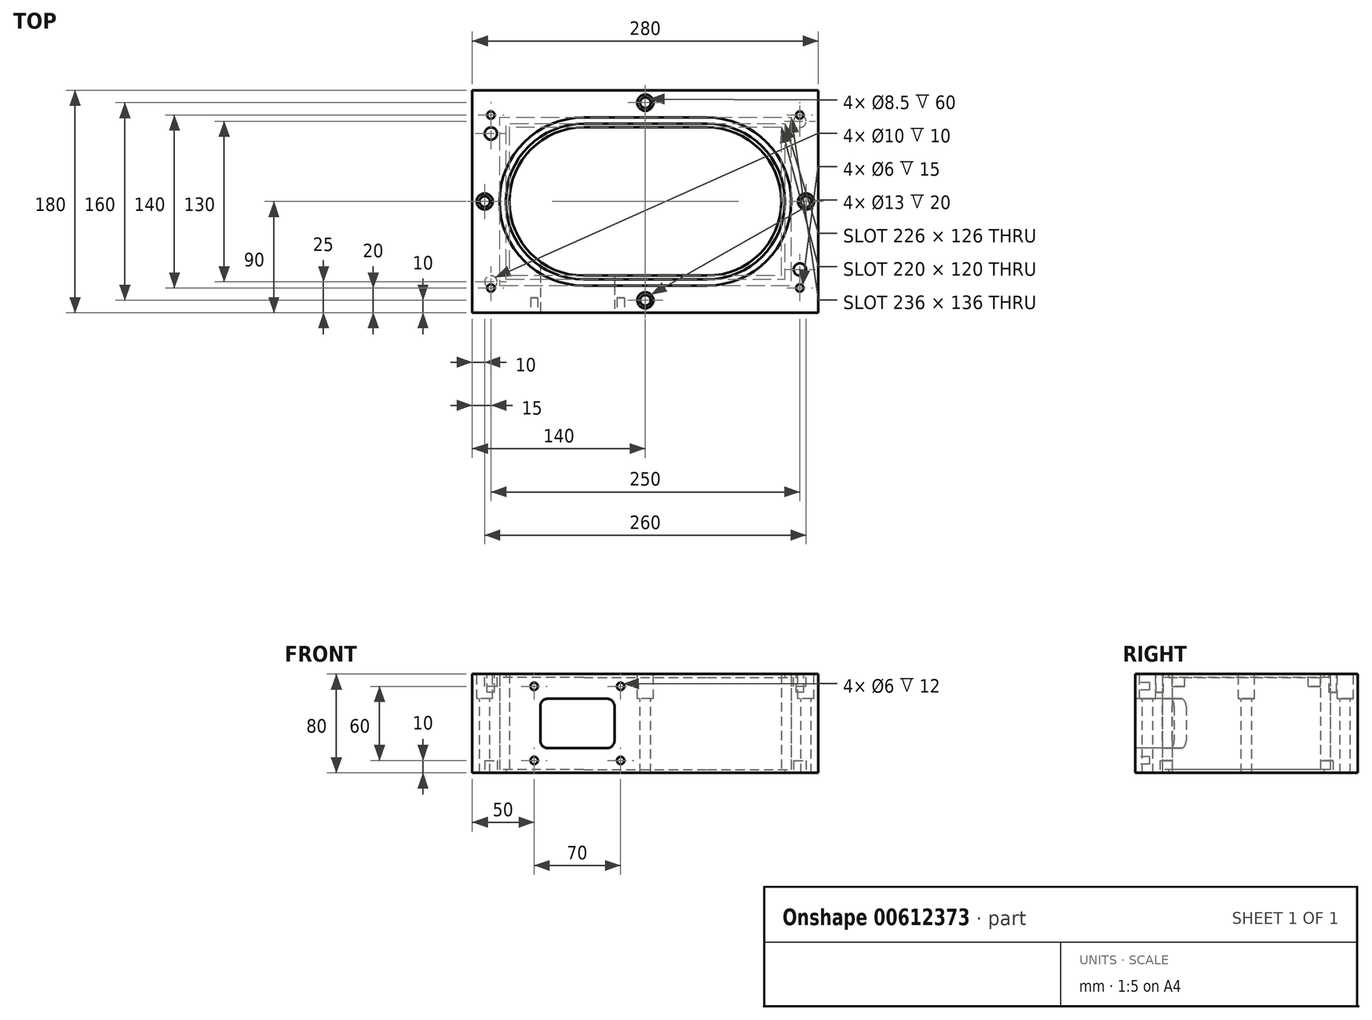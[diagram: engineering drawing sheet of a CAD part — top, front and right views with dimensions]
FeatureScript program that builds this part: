
annotation { "Feature Type Name" : "Feature", "Feature Type Description" : "" }
export const myFeature = defineFeature(function(context is Context, id is Id, definition is map)
    precondition{}
    {
        {
            var Q0;
            Q0=qCreatedBy(makeId("Top.planeOp"),FACE);
            var sketch = newSketch(context, id + "F0", { "sketchPlane" : qUnion([Q0])});
            skLineSegment(sketch, "E0.bottom", {"start": v(-140, 90) * mm, "end": v(140, 90) * mm});
            skLineSegment(sketch, "E0.top", {"start": v(-140, -90) * mm, "end": v(140, -90) * mm});
            skLineSegment(sketch, "E0.left", {"start": v(-140, 90) * mm, "end": v(-140, -90) * mm});
            skLineSegment(sketch, "E0.right", {"start": v(140, 90) * mm, "end": v(140, -90) * mm});
            skArc(sketch, "E1", {"start": v(-50, 60) * mm, "mid": v(-110, 0) * mm, "end": v(-50, -60) * mm});
            skArc(sketch, "E2", {"start": v(50, -60) * mm, "mid": v(110, 0) * mm, "end": v(50, 60) * mm});
            skArc(sketch, "E3", {"start": v(-50, 63) * mm, "mid": v(-113, 0) * mm, "end": v(-50, -63) * mm});
            skArc(sketch, "E4", {"start": v(50, -63) * mm, "mid": v(113, 0) * mm, "end": v(50, 63) * mm});
            skLineSegment(sketch, "E5", {"start": v(-50, 68) * mm, "end": v(50, 68) * mm});
            skLineSegment(sketch, "E6", {"start": v(50, 63) * mm, "end": v(-50, 63) * mm});
            skLineSegment(sketch, "E7", {"start": v(-50, 60) * mm, "end": v(50, 60) * mm});
            skLineSegment(sketch, "E8", {"start": v(-50, -60) * mm, "end": v(50, -60) * mm});
            skLineSegment(sketch, "E9", {"start": v(50, -63) * mm, "end": v(-50, -63) * mm});
            skLineSegment(sketch, "E10", {"start": v(-50, -68) * mm, "end": v(50, -68) * mm});
            skArc(sketch, "E11.trimOffspring", {"start": v(-50, 68) * mm, "mid": v(-118, 0) * mm, "end": v(-50, -68) * mm});
            skArc(sketch, "E12.trimOffspring", {"start": v(50, -68) * mm, "mid": v(118, 0) * mm, "end": v(50, 68) * mm});
            skSolve(sketch);
        }
        {
            var Q0;
            Q0=makeQuery(id+"F0.imprint","IMPRINT",FACE,{"disambiguationData":[TD([[makeQuery(id+"F0.imprint","IMPRINT",EDGE,{"derivedFrom":sQuery(id+"F0.wireOp",EDGE,"E0.bottom")}),-1.0]])]});
            extrude(context, id + "F1", {"entities" : qUnion([Q0]), "depth" : 40 * mm, "offsetDistance" : 25 * mm, "hasSecondDirection" : true, "secondDirectionOppositeDirection" : true, "secondDirectionDepth" : 40 * mm});
        }
        {
            var Q0;
            Q0=makeQuery(id+"F0.imprint","IMPRINT",FACE,{"disambiguationData":[TD([[makeQuery(id+"F0.imprint","IMPRINT",EDGE,{"derivedFrom":sQuery(id+"F0.wireOp",EDGE,"E3")}),-1.0]])]});
            extrude(context, id + "F2", {"entities" : qUnion([Q0]), "depth" : 37.3 * mm, "offsetDistance" : 25 * mm, "hasSecondDirection" : true, "secondDirectionOppositeDirection" : true, "secondDirectionDepth" : 37.3 * mm});
        }
        {
            var Q0;
            Q0=makeQuery(id+"F0.imprint","IMPRINT",FACE,{"disambiguationData":[TD([[makeQuery(id+"F0.imprint","IMPRINT",EDGE,{"derivedFrom":sQuery(id+"F0.wireOp",EDGE,"E1")}),-1.0]])]});
            extrude(context, id + "F3", {"entities" : qUnion([Q0]), "operationType" : NewBodyOperationType.ADD, "depth" : 40 * mm, "offsetDistance" : 25 * mm, "hasSecondDirection" : true, "secondDirectionOppositeDirection" : true, "secondDirectionDepth" : 40 * mm});
        }
        {
            var Q0;
            Q0=makeQuery(id+"F1.opExtrude","CAP_FACE",FACE,{"disambiguationData":[OSD([sQuery(id+"F0.wireOp",EDGE,"E0.bottom"),sQuery(id+"F0.wireOp",EDGE,"E0.top"),sQuery(id+"F0.wireOp",EDGE,"E0.left"),sQuery(id+"F0.wireOp",EDGE,"E0.right"),sQuery(id+"F0.wireOp",EDGE,"E5"),sQuery(id+"F0.wireOp",EDGE,"E10"),sQuery(id+"F0.wireOp",EDGE,"E11.trimOffspring"),sQuery(id+"F0.wireOp",EDGE,"E12.trimOffspring")])],"isStart":false});
            var sketch = newSketch(context, id + "F4", { "sketchPlane" : qUnion([Q0])});
            skCircle(sketch, "E13", {"center": v(-130, 0) * mm, "radius": 6.5 * mm});
            skCircle(sketch, "E14", {"center": v(130, 0) * mm, "radius": 6.5 * mm});
            skCircle(sketch, "E15", {"center": v(0, -80) * mm, "radius": 6.5 * mm});
            skPoint(sketch, "E15.centerSnap0", {"position": v(0, -68) * mm});
            skCircle(sketch, "E16", {"center": v(0, 80) * mm, "radius": 6.5 * mm});
            skCircle(sketch, "E17", {"center": v(-130, 0) * mm, "radius": 4.25 * mm});
            skCircle(sketch, "E18", {"center": v(0, -80) * mm, "radius": 4.25 * mm});
            skCircle(sketch, "E19", {"center": v(130, 0) * mm, "radius": 4.25 * mm});
            skCircle(sketch, "E20", {"center": v(0, 80) * mm, "radius": 4.25 * mm});
            skCircle(sketch, "E21", {"center": v(-125, -70) * mm, "radius": 3 * mm});
            skCircle(sketch, "E22", {"center": v(125, -70) * mm, "radius": 3 * mm});
            skCircle(sketch, "E23", {"center": v(125, 70) * mm, "radius": 3 * mm});
            skCircle(sketch, "E24", {"center": v(-125, 70) * mm, "radius": 3 * mm});
            skCircle(sketch, "E25", {"center": v(-125, 55) * mm, "radius": 5 * mm});
            skCircle(sketch, "E26", {"center": v(125, -55) * mm, "radius": 5 * mm});
            skSolve(sketch);
        }
        {
            var Q0;
            Q0=makeQuery(id+"F4.imprint","IMPRINT",FACE,{"disambiguationData":[TD([[makeQuery(id+"F4.imprint","IMPRINT",EDGE,{"derivedFrom":sQuery(id+"F4.wireOp",EDGE,"E25")}),1.0]])]});
            var Q1;
            Q1=makeQuery(id+"F4.imprint","IMPRINT",FACE,{"disambiguationData":[TD([[makeQuery(id+"F4.imprint","IMPRINT",EDGE,{"derivedFrom":sQuery(id+"F4.wireOp",EDGE,"E26")}),1.0]])]});
            extrude(context, id + "F5", {"entities" : qUnion([Q0, Q1]), "operationType" : NewBodyOperationType.REMOVE, "oppositeDirection" : true, "depth" : 10 * mm, "offsetDistance" : 25 * mm});
        }
        {
            var Q0;
            Q0=makeQuery(id+"F4.imprint","IMPRINT",FACE,{"disambiguationData":[TD([[makeQuery(id+"F4.imprint","IMPRINT",EDGE,{"derivedFrom":sQuery(id+"F4.wireOp",EDGE,"E20")}),1.0]])]});
            var Q1;
            Q1=makeQuery(id+"F4.imprint","IMPRINT",FACE,{"disambiguationData":[TD([[makeQuery(id+"F4.imprint","IMPRINT",EDGE,{"derivedFrom":sQuery(id+"F4.wireOp",EDGE,"E19")}),1.0]])]});
            var Q2;
            Q2=makeQuery(id+"F4.imprint","IMPRINT",FACE,{"disambiguationData":[TD([[makeQuery(id+"F4.imprint","IMPRINT",EDGE,{"derivedFrom":sQuery(id+"F4.wireOp",EDGE,"E18")}),1.0]])]});
            var Q3;
            Q3=makeQuery(id+"F4.imprint","IMPRINT",FACE,{"disambiguationData":[TD([[makeQuery(id+"F4.imprint","IMPRINT",EDGE,{"derivedFrom":sQuery(id+"F4.wireOp",EDGE,"E17")}),1.0]])]});
            extrude(context, id + "F6", {"entities" : qUnion([Q0, Q1, Q2, Q3]), "operationType" : NewBodyOperationType.REMOVE, "oppositeDirection" : true, "depth" : 80 * mm, "offsetDistance" : 25 * mm});
        }
        {
            var Q0;
            Q0=makeQuery(id+"F4.imprint","IMPRINT",FACE,{"disambiguationData":[TD([[makeQuery(id+"F4.imprint","IMPRINT",EDGE,{"derivedFrom":sQuery(id+"F4.wireOp",EDGE,"E24")}),1.0]])]});
            var Q1;
            Q1=makeQuery(id+"F4.imprint","IMPRINT",FACE,{"disambiguationData":[TD([[makeQuery(id+"F4.imprint","IMPRINT",EDGE,{"derivedFrom":sQuery(id+"F4.wireOp",EDGE,"E23")}),1.0]])]});
            var Q2;
            Q2=makeQuery(id+"F4.imprint","IMPRINT",FACE,{"disambiguationData":[TD([[makeQuery(id+"F4.imprint","IMPRINT",EDGE,{"derivedFrom":sQuery(id+"F4.wireOp",EDGE,"E22")}),1.0]])]});
            var Q3;
            Q3=makeQuery(id+"F4.imprint","IMPRINT",FACE,{"disambiguationData":[TD([[makeQuery(id+"F4.imprint","IMPRINT",EDGE,{"derivedFrom":sQuery(id+"F4.wireOp",EDGE,"E21")}),1.0]])]});
            extrude(context, id + "F7", {"entities" : qUnion([Q0, Q1, Q2, Q3]), "operationType" : NewBodyOperationType.REMOVE, "oppositeDirection" : true, "depth" : 15 * mm, "offsetDistance" : 25 * mm});
        }
        {
            var Q0;
            Q0=makeQuery(id+"F4.imprint","IMPRINT",FACE,{"disambiguationData":[TD([[makeQuery(id+"F4.imprint","IMPRINT",EDGE,{"derivedFrom":sQuery(id+"F4.wireOp",EDGE,"E16")}),1.0]])]});
            var Q1;
            Q1=makeQuery(id+"F4.imprint","IMPRINT",FACE,{"disambiguationData":[TD([[makeQuery(id+"F4.imprint","IMPRINT",EDGE,{"derivedFrom":sQuery(id+"F4.wireOp",EDGE,"E14")}),1.0]])]});
            var Q2;
            Q2=makeQuery(id+"F4.imprint","IMPRINT",FACE,{"disambiguationData":[TD([[makeQuery(id+"F4.imprint","IMPRINT",EDGE,{"derivedFrom":sQuery(id+"F4.wireOp",EDGE,"E15")}),1.0]])]});
            var Q3;
            Q3=makeQuery(id+"F4.imprint","IMPRINT",FACE,{"disambiguationData":[TD([[makeQuery(id+"F4.imprint","IMPRINT",EDGE,{"derivedFrom":sQuery(id+"F4.wireOp",EDGE,"E13")}),1.0]])]});
            extrude(context, id + "F8", {"entities" : qUnion([Q0, Q1, Q2, Q3]), "operationType" : NewBodyOperationType.REMOVE, "oppositeDirection" : true, "depth" : 20 * mm, "offsetDistance" : 25 * mm});
        }
        {
            var Q0;
            Q0=makeQuery(id+"F1.opExtrude","SWEPT_FACE",FACE,{"disambiguationData":[OSD([sQuery(id+"F0.wireOp",EDGE,"E0.top")])]});
            var sketch = newSketch(context, id + "F9", { "sketchPlane" : qUnion([Q0])});
            skLineSegment(sketch, "E27.bottom", {"start": v(-79, 20) * mm, "end": v(-31, 20) * mm});
            skLineSegment(sketch, "E27.top", {"start": v(-79, -20) * mm, "end": v(-31, -20) * mm});
            skLineSegment(sketch, "E27.left", {"start": v(-85, 14) * mm, "end": v(-85, -14) * mm});
            skLineSegment(sketch, "E27.right", {"start": v(-25, 14) * mm, "end": v(-25, -14) * mm});
            skCircle(sketch, "E28", {"center": v(-90, 30) * mm, "radius": 3 * mm});
            skCircle(sketch, "E29", {"center": v(-20, 30) * mm, "radius": 3 * mm});
            skCircle(sketch, "E30", {"center": v(-90, -30) * mm, "radius": 3 * mm});
            skCircle(sketch, "E31", {"center": v(-20, -30) * mm, "radius": 3 * mm});
            skPoint(sketch, "E32.visualSharp", {"position": v(-85, 20) * mm});
            skArc(sketch, "E32.filletArc", {"start": v(-79, 20) * mm, "mid": v(-83.24, 18.24) * mm, "end": v(-85, 14) * mm});
            skPoint(sketch, "E33.visualSharp", {"position": v(-25, 20) * mm});
            skArc(sketch, "E33.filletArc", {"start": v(-25, 14) * mm, "mid": v(-26.76, 18.24) * mm, "end": v(-31, 20) * mm});
            skPoint(sketch, "E34.visualSharp", {"position": v(-25, -20) * mm});
            skArc(sketch, "E34.filletArc", {"start": v(-31, -20) * mm, "mid": v(-26.76, -18.24) * mm, "end": v(-25, -14) * mm});
            skPoint(sketch, "E35.visualSharp", {"position": v(-85, -20) * mm});
            skArc(sketch, "E35.filletArc", {"start": v(-85, -14) * mm, "mid": v(-83.24, -18.24) * mm, "end": v(-79, -20) * mm});
            skSolve(sketch);
        }
        {
            var Q0;
            Q0=makeQuery(id+"F9.imprint","IMPRINT",FACE,{"disambiguationData":[TD([[makeQuery(id+"F9.imprint","IMPRINT",EDGE,{"derivedFrom":sQuery(id+"F9.wireOp",EDGE,"E28")}),1.0]])]});
            var Q1;
            Q1=makeQuery(id+"F9.imprint","IMPRINT",FACE,{"disambiguationData":[TD([[makeQuery(id+"F9.imprint","IMPRINT",EDGE,{"derivedFrom":sQuery(id+"F9.wireOp",EDGE,"E29")}),1.0]])]});
            var Q2;
            Q2=makeQuery(id+"F9.imprint","IMPRINT",FACE,{"disambiguationData":[TD([[makeQuery(id+"F9.imprint","IMPRINT",EDGE,{"derivedFrom":sQuery(id+"F9.wireOp",EDGE,"E31")}),1.0]])]});
            var Q3;
            Q3=makeQuery(id+"F9.imprint","IMPRINT",FACE,{"disambiguationData":[TD([[makeQuery(id+"F9.imprint","IMPRINT",EDGE,{"derivedFrom":sQuery(id+"F9.wireOp",EDGE,"E30")}),1.0]])]});
            extrude(context, id + "F10", {"entities" : qUnion([Q0, Q1, Q2, Q3]), "operationType" : NewBodyOperationType.REMOVE, "oppositeDirection" : true, "depth" : 12 * mm, "offsetDistance" : 25 * mm});
        }
        {
            var Q0;
            Q0=makeQuery(id+"F9.imprint","IMPRINT",FACE,{"disambiguationData":[TD([[makeQuery(id+"F9.imprint","IMPRINT",EDGE,{"derivedFrom":sQuery(id+"F9.wireOp",EDGE,"E27.bottom")}),-1.0]])]});
            extrude(context, id + "F11", {"entities" : qUnion([Q0]), "operationType" : NewBodyOperationType.REMOVE, "oppositeDirection" : true, "depth" : 45 * mm, "offsetDistance" : 25 * mm});
        }
        {
            var Q0;
            Q0=makeQuery(id+"F1.opExtrude","CAP_FACE",FACE,{"disambiguationData":[OSD([sQuery(id+"F0.wireOp",EDGE,"E0.bottom"),sQuery(id+"F0.wireOp",EDGE,"E0.top"),sQuery(id+"F0.wireOp",EDGE,"E0.left"),sQuery(id+"F0.wireOp",EDGE,"E0.right"),sQuery(id+"F0.wireOp",EDGE,"E5"),sQuery(id+"F0.wireOp",EDGE,"E10"),sQuery(id+"F0.wireOp",EDGE,"E11.trimOffspring"),sQuery(id+"F0.wireOp",EDGE,"E12.trimOffspring")])],"isStart":true});
            var sketch = newSketch(context, id + "F12", { "sketchPlane" : qUnion([Q0])});
            skCircle(sketch, "E36", {"center": v(-125, 65) * mm, "radius": 5 * mm});
            skCircle(sketch, "E37", {"center": v(125, -65) * mm, "radius": 5 * mm});
            skSolve(sketch);
        }
        {
            var Q0;
            Q0=makeQuery(id+"F12.imprint","IMPRINT",FACE,{"disambiguationData":[TD([[makeQuery(id+"F12.imprint","IMPRINT",EDGE,{"derivedFrom":sQuery(id+"F12.wireOp",EDGE,"E36")}),1.0]])]});
            var Q1;
            Q1=makeQuery(id+"F12.imprint","IMPRINT",FACE,{"disambiguationData":[TD([[makeQuery(id+"F12.imprint","IMPRINT",EDGE,{"derivedFrom":sQuery(id+"F12.wireOp",EDGE,"E37")}),1.0]])]});
            extrude(context, id + "F13", {"entities" : qUnion([Q0, Q1]), "operationType" : NewBodyOperationType.REMOVE, "oppositeDirection" : true, "depth" : 10 * mm, "offsetDistance" : 25 * mm});
        }
    });
